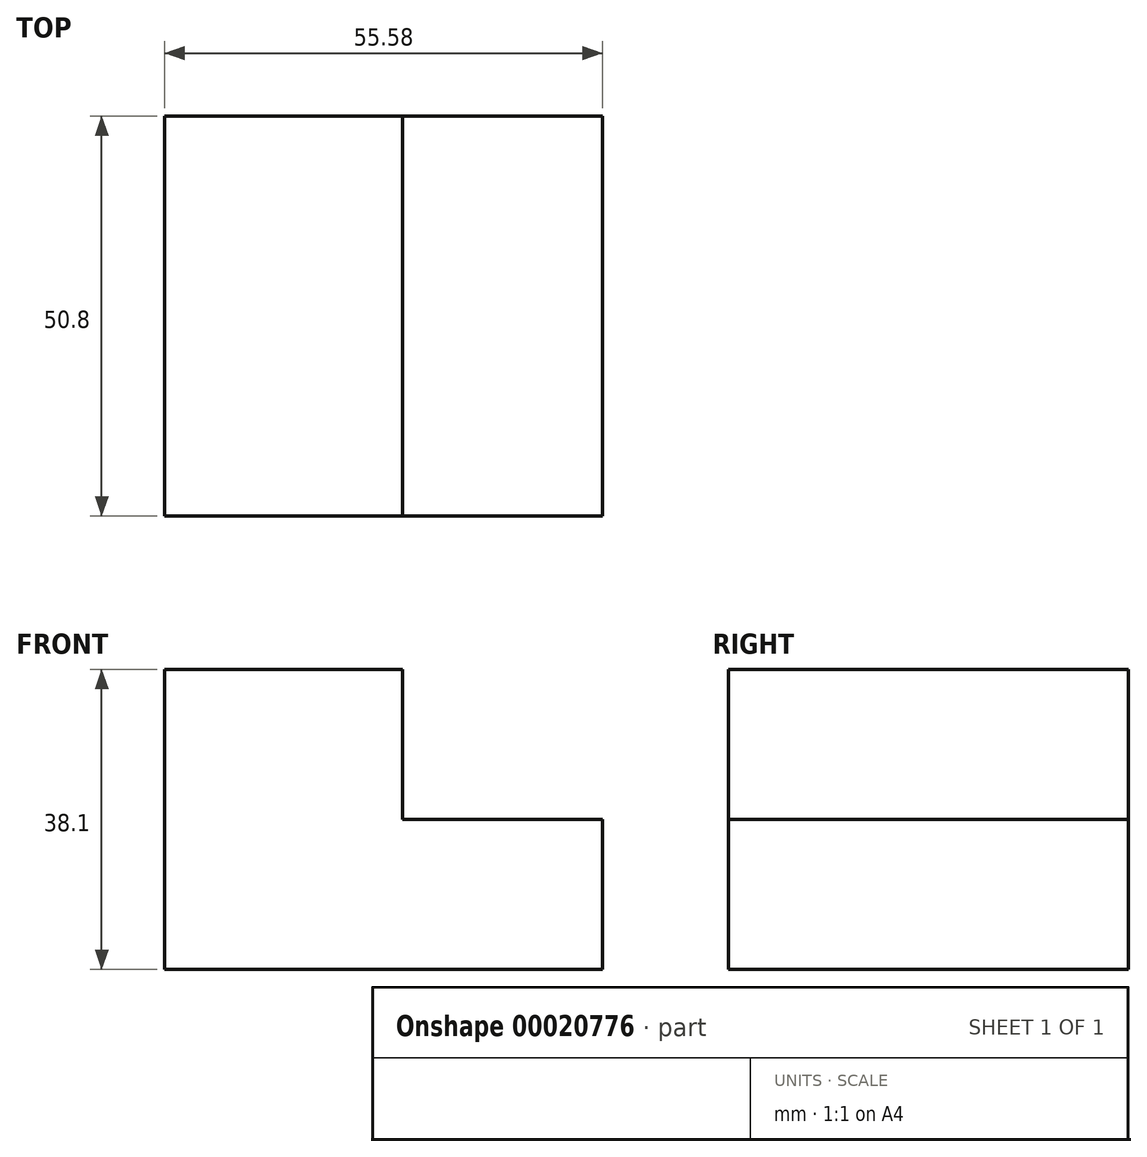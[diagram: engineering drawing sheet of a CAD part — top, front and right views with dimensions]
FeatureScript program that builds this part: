
annotation { "Feature Type Name" : "Feature", "Feature Type Description" : "" }
export const myFeature = defineFeature(function(context is Context, id is Id, definition is map)
    precondition{}
    {
        {
            var Q0;
            Q0=qCreatedBy(makeId("Front.planeOp"),FACE);
            var sketch = newSketch(context, id + "F0", { "sketchPlane" : qUnion([Q0])});
            skLineSegment(sketch, "E0.bottom", {"start": v(0, 0) * mm, "end": v(55.58, 0) * mm});
            skLineSegment(sketch, "E0.top", {"start": v(0, 38.1) * mm, "end": v(30.18, 38.1) * mm});
            skLineSegment(sketch, "E0.left", {"start": v(0, 0) * mm, "end": v(0, 38.1) * mm});
            skLineSegment(sketch, "E0.right", {"start": v(55.58, 0) * mm, "end": v(55.58, 19.05) * mm});
            skLineSegment(sketch, "E1", {"start": v(30.18, 38.1) * mm, "end": v(30.18, 19.05) * mm});
            skLineSegment(sketch, "E2", {"start": v(30.18, 19.05) * mm, "end": v(55.58, 19.05) * mm});
            skSolve(sketch);
        }
        {
            var Q0;
            Q0=makeQuery(id+"F0.imprint","IMPRINT",FACE,{"disambiguationData":[TD([[makeQuery(id+"F0.imprint","IMPRINT",EDGE,{"derivedFrom":sQuery(id+"F0.wireOp",EDGE,"E0.bottom")}),1.0]])]});
            extrude(context, id + "F1", {"entities" : qUnion([Q0]), "depth" : 50.8 * mm});
        }
    });
